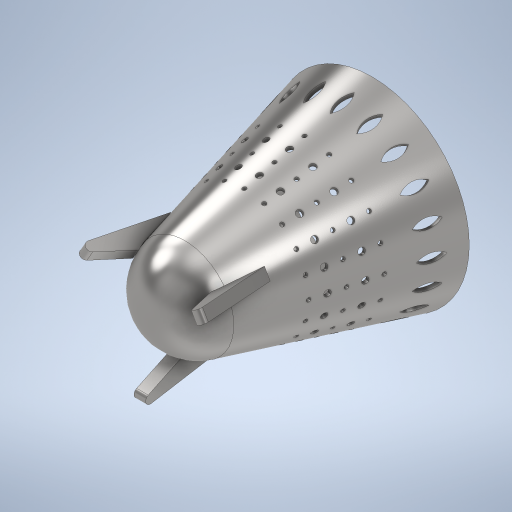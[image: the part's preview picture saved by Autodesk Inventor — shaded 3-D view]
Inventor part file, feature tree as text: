
AUTODESK INVENTOR PART (.ipt)
format: ipt  version: 2024 (Build 280153000, 153)  size: 951,296 bytes
history: native  units: mm
features: sketch x4, other x4, pattern_circular x4, plane x3, extrude x2, hole x2, pattern_linear x2, revolve x1, shell x1
ambient origin geometry x8: Origin, YZ Plane, XZ Plane, XY Plane, X Axis, Y Axis, Z Axis, Center Point
bodies: Volumenkörper1 (feature_tree)
feature tree (23):
  revolve  "Umdrehung1"
  shell  "Wandung1"  Thickness=250.0mm
  plane  "Arbeitsebene1"
  sketch  "Skizze2"  dims[d3=90.0deg d4=5.0mm]
  other  "Arbeitsachse3"
  plane  "Arbeitsebene3"
  other  "Arbeitsachse4"
  other  "Arbeitsachse5"
  sketch  "Skizze3"  dims[d5=0.0mm d9=90.0mm d10=40.0mm]
  extrude  "Extrusion1"  Depth=65.0mm
  hole  "Bohrung1"  [1 undecoded]
  hole  "Bohrung2"  [1 undecoded]
  pattern_circular  "Runde Anordnung1"  Count=4  [1 undecoded]
  pattern_linear  "Rechteckige Anordnung1"  Count1=2  [1 undecoded]
  pattern_circular  "Runde Anordnung2"  [2 undecoded]
  pattern_linear  "Rechteckige Anordnung2"  Spacing1=10.0mm  [1 undecoded]
  pattern_circular  "Runde Anordnung3"  Count=20 Angle=360.0deg
  plane  "Arbeitsebene5"
  extrude  "Extrusion2"  Depth=15.0mm
  pattern_circular  "Runde Anordnung4"  Count=20 Angle=360.0deg
  sketch  "Skizze1"  dims[d1=65.0mm d2=225.0mm]
  other  "Arbeitspunkt4"
  sketch  "Skizze5"  dims[d11=32.0mm d12=20.0mm d13=25.0mm d14=10.0mm d15=0.0mm d16=5.0mm d17=6.0mm d18=4.0mm d19=2.0mm d20=90.0deg d21=6.0mm d22=20.594885mm d23=8.0mm d24=6.0mm d25=4.0mm d26=2.0mm d27=90.0deg d28=6.0mm d29=0.0mm d30=200.0mm d31=360.0deg d33=30.0mm d35=40.0mm d36=200.0mm d37=360.0deg d39=20.0mm d41=40.0mm d42=200.0mm d43=360.0deg d45=0.0mm d51=45.0mm d52=100.0mm d53=6.0mm d54=299.0mm d55=2.792527mm d56=15.0mm d57=0.0mm d58=30.0mm d59=360.0deg]
note: 7 required parameter values undecoded (feature->parameter linkage not recoverable at this tier; creation-order binding heuristic only, values carry confidence <= 0.55)
